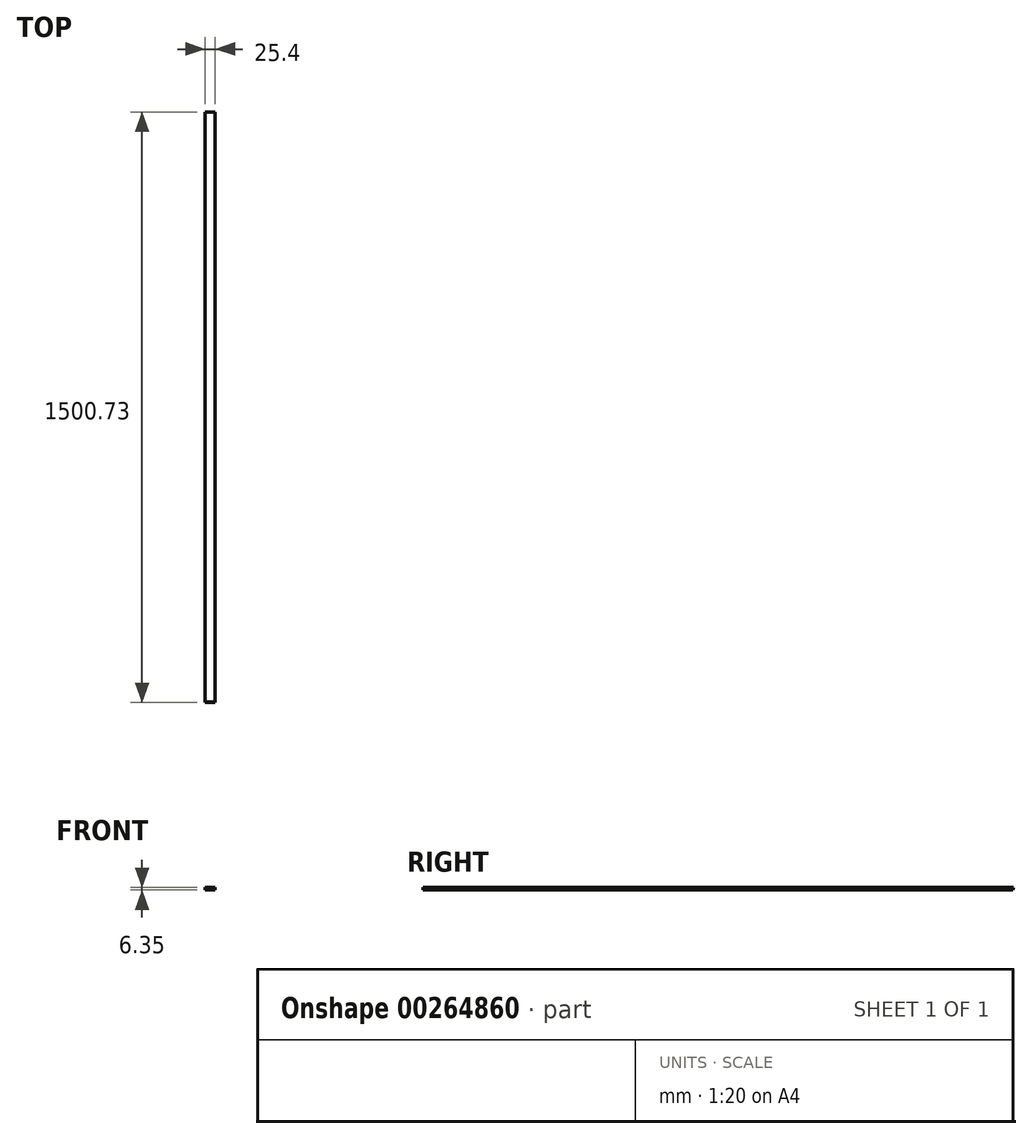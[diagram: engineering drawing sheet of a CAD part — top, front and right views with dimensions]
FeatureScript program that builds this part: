
annotation { "Feature Type Name" : "Feature", "Feature Type Description" : "" }
export const myFeature = defineFeature(function(context is Context, id is Id, definition is map)
    precondition{}
    {
        {
            var Q0;
            Q0=qCreatedBy(makeId("Top.planeOp"),FACE);
            var sketch = newSketch(context, id + "F0", { "sketchPlane" : qUnion([Q0])});
            skLineSegment(sketch, "E0.bottom", {"start": v(0, 0) * mm, "end": v(25.4, 0) * mm});
            skLineSegment(sketch, "E0.top", {"start": v(0, 1500.73) * mm, "end": v(25.4, 1500.73) * mm});
            skLineSegment(sketch, "E0.left", {"start": v(0, 0) * mm, "end": v(0, 1500.73) * mm});
            skLineSegment(sketch, "E0.right", {"start": v(25.4, 0) * mm, "end": v(25.4, 1500.73) * mm});
            skSolve(sketch);
        }
        {
            var Q0;
            Q0=makeQuery(id+"F0.imprint","IMPRINT",FACE,{"disambiguationData":[TD([[makeQuery(id+"F0.imprint","IMPRINT",EDGE,{"derivedFrom":sQuery(id+"F0.wireOp",EDGE,"E0.bottom")}),1.0]])]});
            extrude(context, id + "F1", {"entities" : qUnion([Q0]), "depth" : 6.35 * mm, "offsetDistance" : 25.4 * mm});
        }
        {
            var Q0;
            Q0=makeQuery(id+"F1.opExtrude","SWEPT_FACE",FACE,{"disambiguationData":[OSD([sQuery(id+"F0.wireOp",EDGE,"E0.right")])]});
            var sketch = newSketch(context, id + "F2", { "sketchPlane" : qUnion([Q0])});
            skLineSegment(sketch, "E1", {"start": v(0, 15.23) * mm, "end": v(0, 0) * mm});
            skLineSegment(sketch, "E2", {"start": v(0, 0) * mm, "end": v(2.69, 15.23) * mm});
            skLineSegment(sketch, "E3", {"start": v(2.69, 15.23) * mm, "end": v(0, 15.23) * mm});
            skLineSegment(sketch, "E4", {"start": v(1500.73, 6.35) * mm, "end": v(1500.73, 6.35) * mm});
            skLineSegment(sketch, "E5", {"start": v(1500.73, 6.35) * mm, "end": v(1500.73, -6.32) * mm});
            skLineSegment(sketch, "E6", {"start": v(1500.73, -6.32) * mm, "end": v(1497.34, -6.32) * mm});
            skLineSegment(sketch, "E7", {"start": v(1497.34, -6.32) * mm, "end": v(1500.73, 6.35) * mm});
            skSolve(sketch);
        }
        {
            var Q0;
            {var subQ0=sQuery(id+"F2.wireOp",EDGE,"E4");var subQ1=sQuery(id+"F0.wireOp",EDGE,"E0.right");var subQ2=makeQuery(id+"F1.opExtrude","CAP_EDGE",EDGE,{"disambiguationData":[OSD([subQ1])],"isStart":true});var subQ3=makeQuery(id+"F2.imprint","INTERSECT",VERTEX,{"derivedFrom":[subQ2,subQ0]});Q0=makeQuery(id+"F2.imprint","IMPRINT",FACE,{"disambiguationData":[TD([[makeQuery(id+"F2.imprint","IMPRINT",EDGE,{"disambiguationData":[TD([[subQ3,1.0]])],"derivedFrom":subQ2}),1.0]])]});}
            var Q1;
            {var subQ1=sQuery(id+"F2.wireOp",EDGE,"E1");var subQ2=sQuery(id+"F0.wireOp",EDGE,"E0.right");var subQ4=makeQuery(id+"F1.opExtrude","CAP_EDGE",EDGE,{"disambiguationData":[OSD([subQ2])],"isStart":false});var subQ5=makeQuery(id+"F2.imprint","INTERSECT",VERTEX,{"derivedFrom":[subQ4,subQ1]});Q1=makeQuery(id+"F2.imprint","IMPRINT",FACE,{"disambiguationData":[TD([[makeQuery(id+"F2.imprint","IMPRINT",EDGE,{"disambiguationData":[TD([[subQ5,-1.0]])],"derivedFrom":subQ4}),-1.0]])]});}
            extrude(context, id + "F3", {"entities" : qUnion([Q0, Q1]), "operationType" : NewBodyOperationType.REMOVE, "endBound" : BoundingType.THROUGH_ALL, "oppositeDirection" : true, "depth" : 25.4 * mm, "offsetDistance" : 25.4 * mm});
        }
    });
